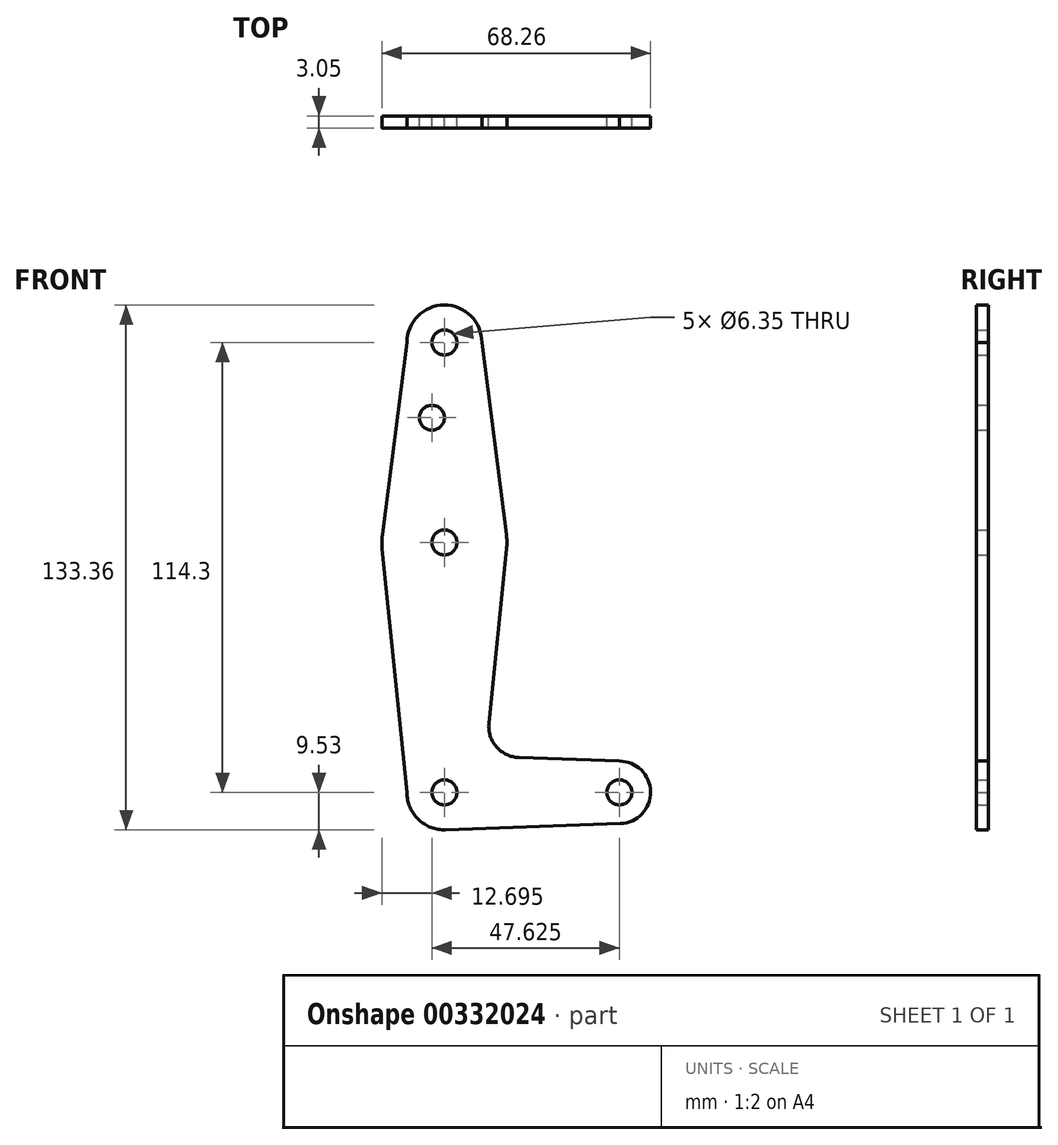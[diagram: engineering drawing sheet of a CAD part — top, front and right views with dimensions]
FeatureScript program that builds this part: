
annotation { "Feature Type Name" : "Feature", "Feature Type Description" : "" }
export const myFeature = defineFeature(function(context is Context, id is Id, definition is map)
    precondition{}
    {
        {
            var Q0;
            Q0=qCreatedBy(makeId("Front.planeOp"),FACE);
            var sketch = newSketch(context, id + "F0", { "sketchPlane" : qUnion([Q0])});
            skLineSegment(sketch, "E0", {"start": v(0, 0) * mm, "end": v(0, 114.3) * mm, "construction": true});
            skLineSegment(sketch, "E1", {"start": v(0, 0) * mm, "end": v(44.45, 0) * mm, "construction": true});
            skCircle(sketch, "E2", {"center": v(0, 114.3) * mm, "radius": 9.53 * mm});
            skCircle(sketch, "E3", {"center": v(0, 63.5) * mm, "radius": 15.88 * mm});
            skCircle(sketch, "E4", {"center": v(0, 0) * mm, "radius": 9.53 * mm});
            skCircle(sketch, "E5", {"center": v(44.45, 0) * mm, "radius": 7.94 * mm});
            skLineSegment(sketch, "E6", {"start": v(-9.53, 114.3) * mm, "end": v(-15.75, 65.5) * mm});
            skLineSegment(sketch, "E7", {"start": v(9.53, 114.3) * mm, "end": v(15.75, 65.5) * mm});
            skLineSegment(sketch, "E8", {"start": v(15.8, 61.9) * mm, "end": v(11.3, 17.6) * mm});
            skLineSegment(sketch, "E9", {"start": v(-15.8, 61.9) * mm, "end": v(-9.52, 0) * mm});
            skLineSegment(sketch, "E10", {"start": v(44.45, 7.94) * mm, "end": v(18.93, 8.85) * mm});
            skCircle(sketch, "E11", {"center": v(0, 114.3) * mm, "radius": 3.18 * mm});
            skCircle(sketch, "E12", {"center": v(0, 63.5) * mm, "radius": 3.18 * mm});
            skCircle(sketch, "E13", {"center": v(0, 0) * mm, "radius": 3.18 * mm});
            skCircle(sketch, "E14", {"center": v(44.45, 0) * mm, "radius": 3.18 * mm});
            skCircle(sketch, "E15", {"center": v(-3.18, 95.2) * mm, "radius": 3.18 * mm});
            skPoint(sketch, "E16.newPointA", {"position": v(9.52, 0) * mm});
            skArc(sketch, "E16.filletArc", {"start": v(11.3, 17.6) * mm, "mid": v(13.22, 11.57) * mm, "end": v(18.93, 8.85) * mm});
            skLineSegment(sketch, "E17", {"start": v(0.34, -9.52) * mm, "end": v(44.73, -7.93) * mm});
            skSolve(sketch);
        }
        {
            var Q0;
            Q0 = qSketchRegion(id + "F0", true);
            extrude(context, id + "F1", {"entities" : qUnion([Q0]), "depth" : 3.05 * mm});
        }
    });
